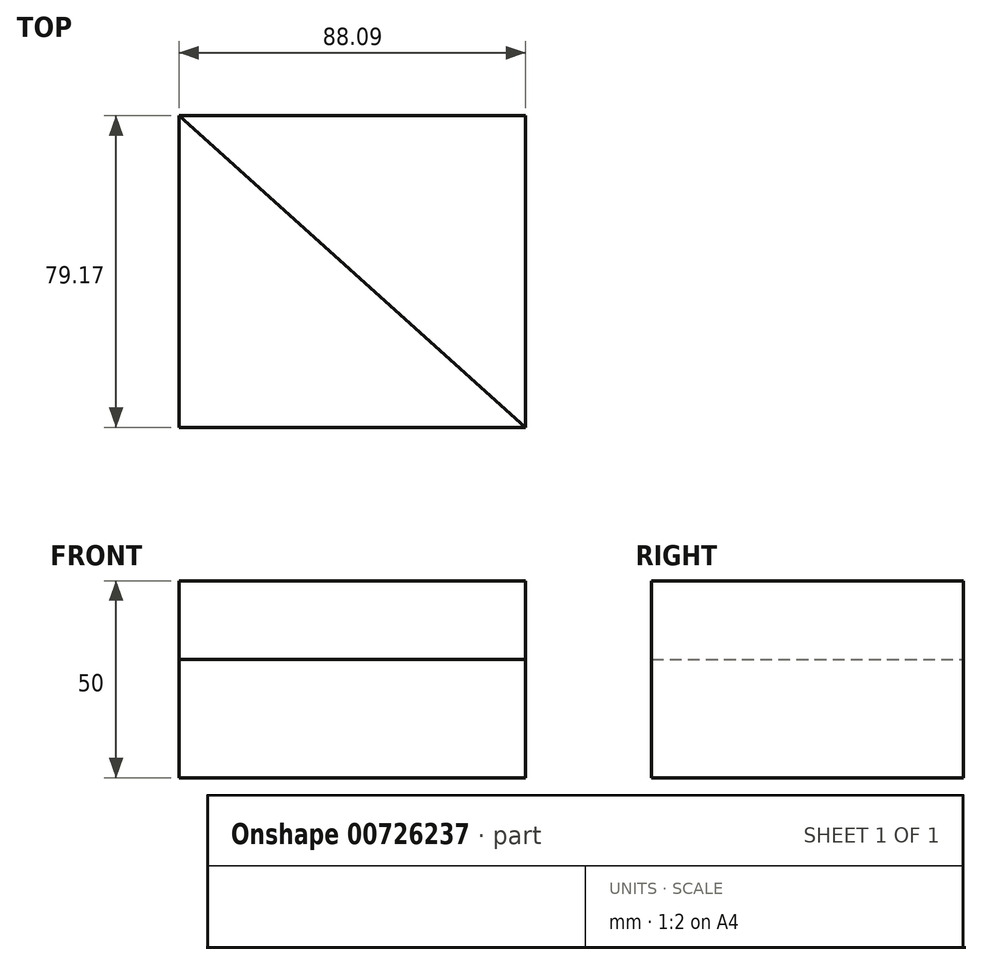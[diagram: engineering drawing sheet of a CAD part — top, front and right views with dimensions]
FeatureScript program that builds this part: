
annotation { "Feature Type Name" : "Feature", "Feature Type Description" : "" }
export const myFeature = defineFeature(function(context is Context, id is Id, definition is map)
    precondition{}
    {
        {
            var Q0;
            Q0=qCreatedBy(makeId("Top.planeOp"),FACE);
            var sketch = newSketch(context, id + "F0", { "sketchPlane" : qUnion([Q0])});
            skLineSegment(sketch, "E0.bottom", {"start": v(-30.15, -28.58) * mm, "end": v(57.94, -28.58) * mm});
            skLineSegment(sketch, "E0.top", {"start": v(-30.15, 50.59) * mm, "end": v(57.94, 50.59) * mm});
            skLineSegment(sketch, "E0.left", {"start": v(-30.15, -28.58) * mm, "end": v(-30.15, 50.59) * mm});
            skLineSegment(sketch, "E0.right", {"start": v(57.94, -28.58) * mm, "end": v(57.94, 50.59) * mm});
            skSolve(sketch);
        }
        {
            var Q0;
            Q0=makeQuery(id+"F0.imprint","IMPRINT",FACE,{"disambiguationData":[TD([[makeQuery(id+"F0.imprint","IMPRINT",EDGE,{"derivedFrom":sQuery(id+"F0.wireOp",EDGE,"E0.bottom")}),1.0]])]});
            extrude(context, id + "F1", {"entities" : qUnion([Q0]), "depth" : 30 * mm, "offsetDistance" : 25.4 * mm});
        }
        {
            var Q0;
            Q0=makeQuery(id+"F1.opExtrude","CAP_FACE",FACE,{"disambiguationData":[OSD([sQuery(id+"F0.wireOp",EDGE,"E0.bottom"),sQuery(id+"F0.wireOp",EDGE,"E0.top"),sQuery(id+"F0.wireOp",EDGE,"E0.left"),sQuery(id+"F0.wireOp",EDGE,"E0.right")])],"isStart":false});
            var sketch = newSketch(context, id + "F2", { "sketchPlane" : qUnion([Q0])});
            skLineSegment(sketch, "E1", {"start": v(-30.15, 50.59) * mm, "end": v(57.94, -28.58) * mm});
            skSolve(sketch);
        }
        {
            var Q0;
            Q0=makeQuery(id+"F2.imprint","IMPRINT",FACE,{"disambiguationData":[TD([[makeQuery(id+"F2.imprint","IMPRINT",EDGE,{"derivedFrom":sQuery(id+"F2.wireOp",EDGE,"E1")}),1.0]])]});
            extrude(context, id + "F3", {"entities" : qUnion([Q0]), "operationType" : NewBodyOperationType.ADD, "depth" : 20 * mm, "offsetDistance" : 25.4 * mm});
        }
    });
